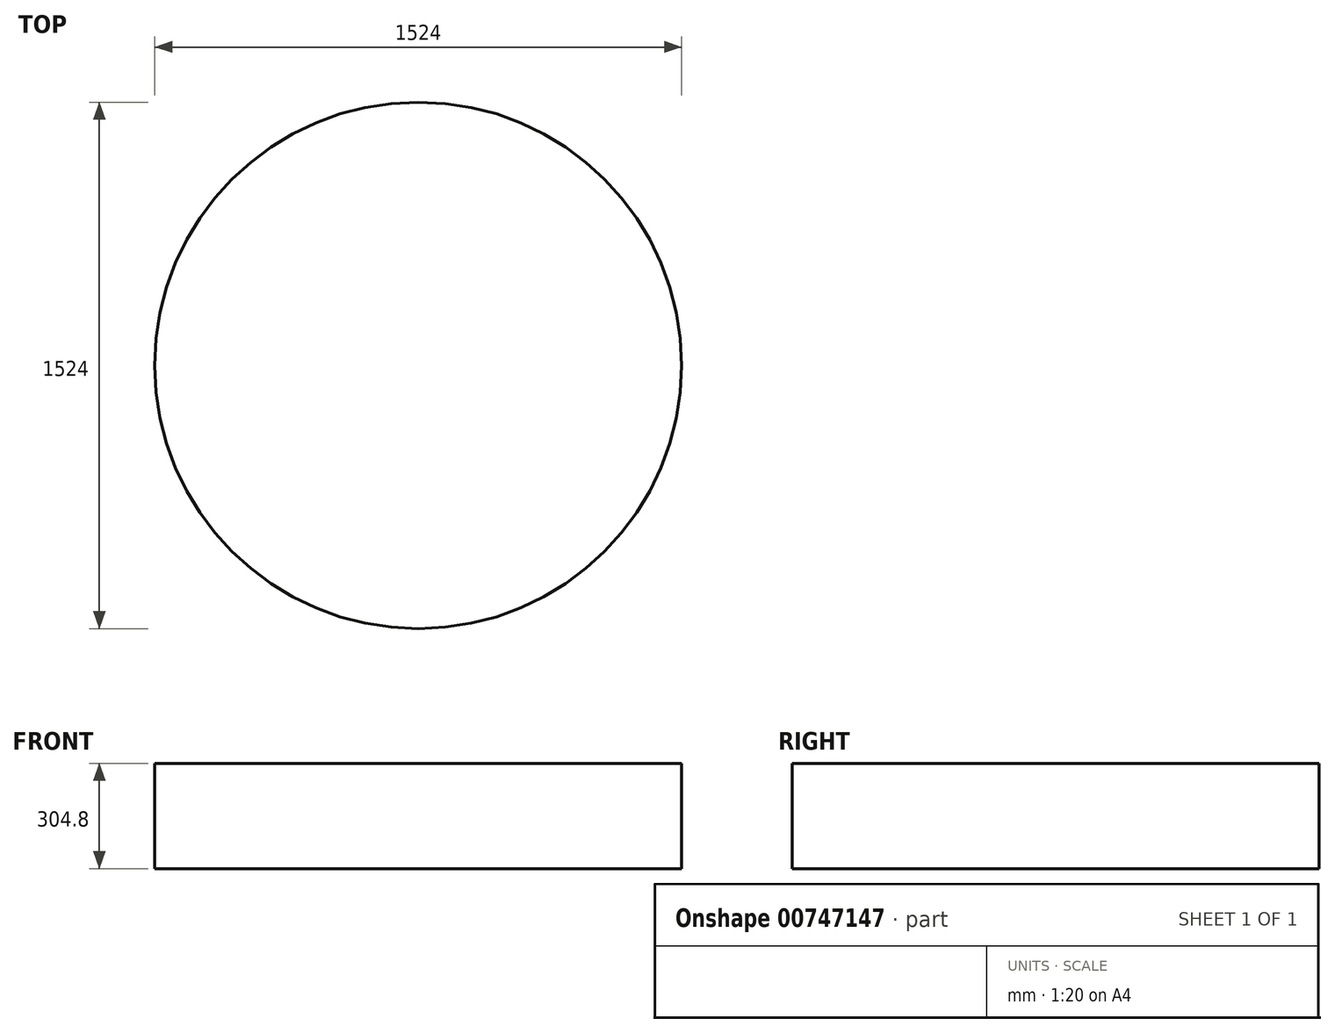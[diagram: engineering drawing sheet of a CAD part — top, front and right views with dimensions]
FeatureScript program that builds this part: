
annotation { "Feature Type Name" : "Feature", "Feature Type Description" : "" }
export const myFeature = defineFeature(function(context is Context, id is Id, definition is map)
    precondition{}
    {
        {
            var Q0;
            Q0=qCreatedBy(makeId("Top.planeOp"),FACE);
            var sketch = newSketch(context, id + "F0", { "sketchPlane" : qUnion([Q0])});
            skCircle(sketch, "E0", {"center": v(0, 0) * mm, "radius": 762 * mm});
            skSolve(sketch);
        }
        {
            var Q0;
            Q0=makeQuery(id+"F0.imprint","IMPRINT",FACE,{"disambiguationData":[TD([[makeQuery(id+"F0.imprint","IMPRINT",EDGE,{"derivedFrom":sQuery(id+"F0.wireOp",EDGE,"E0")}),1.0]])]});
            extrude(context, id + "F1", {"entities" : qUnion([Q0]), "depth" : 304.8 * mm, "offsetDistance" : 25.4 * mm});
        }
    });
